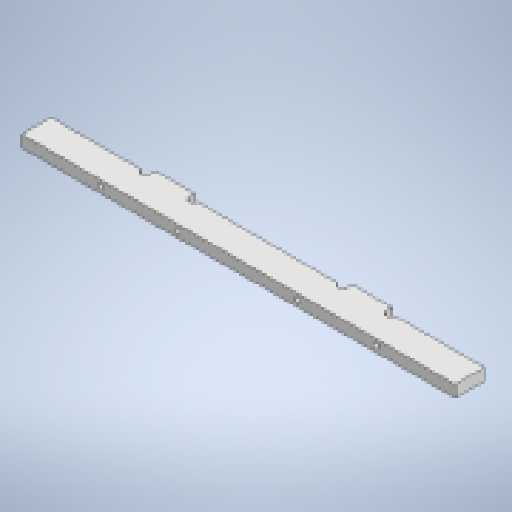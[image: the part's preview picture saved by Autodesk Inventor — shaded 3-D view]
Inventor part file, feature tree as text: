
AUTODESK INVENTOR PART (.ipt)
format: ipt  version: 2024 (Build 280153000, 153)  size: 230,400 bytes
history: native  units: mm
features: reference x12, other x6, sketch x5, extrude x5, hole x1, projected_geometry x1
ambient origin geometry x8: Origin, YZ Plane, XZ Plane, XY Plane, X Axis, Y Axis, Z Axis, Center Point
bodies: Body1 (feature_tree)
feature tree (30):
  other  "ソリッド1"
  sketch  "スケッチ1"
  other  "作業平面1"
  extrude  "押し出し1"  Depth=3.0mm
  sketch  "スケッチ2"
  other  "作業平面2"
  extrude  "押し出し2"  Depth=111.0mm
  extrude  "押し出し3"  Depth=10.0mm TaperAngle=0.0deg
  hole  "穴1"  [1 undecoded]
  sketch  "スケッチ5"
  extrude  "押し出し4"  Depth=2.2mm
  extrude  "押し出し5"  Depth=2.2mm
  reference  "参照1"
  reference  "参照2"
  reference  "参照3"
  reference  "参照4"
  reference  "参照5"
  sketch  "スケッチ3"
  reference  "参照6"
  reference  "参照7"
  reference  "参照8"
  sketch  "スケッチ4"
  reference  "参照9"
  reference  "参照10"
  reference  "参照11"
  reference  "参照12"
  projected_geometry  "投影ループ1"
  other  "<userpath>\OneDrive\ドキュメント\Inventor\Vixen\leg.iam"
  other  "leg.iam"
  other  "side_ita:1"
note: 1 required parameter value undecoded (feature->parameter linkage not recoverable at this tier; creation-order binding heuristic only, values carry confidence <= 0.55)
